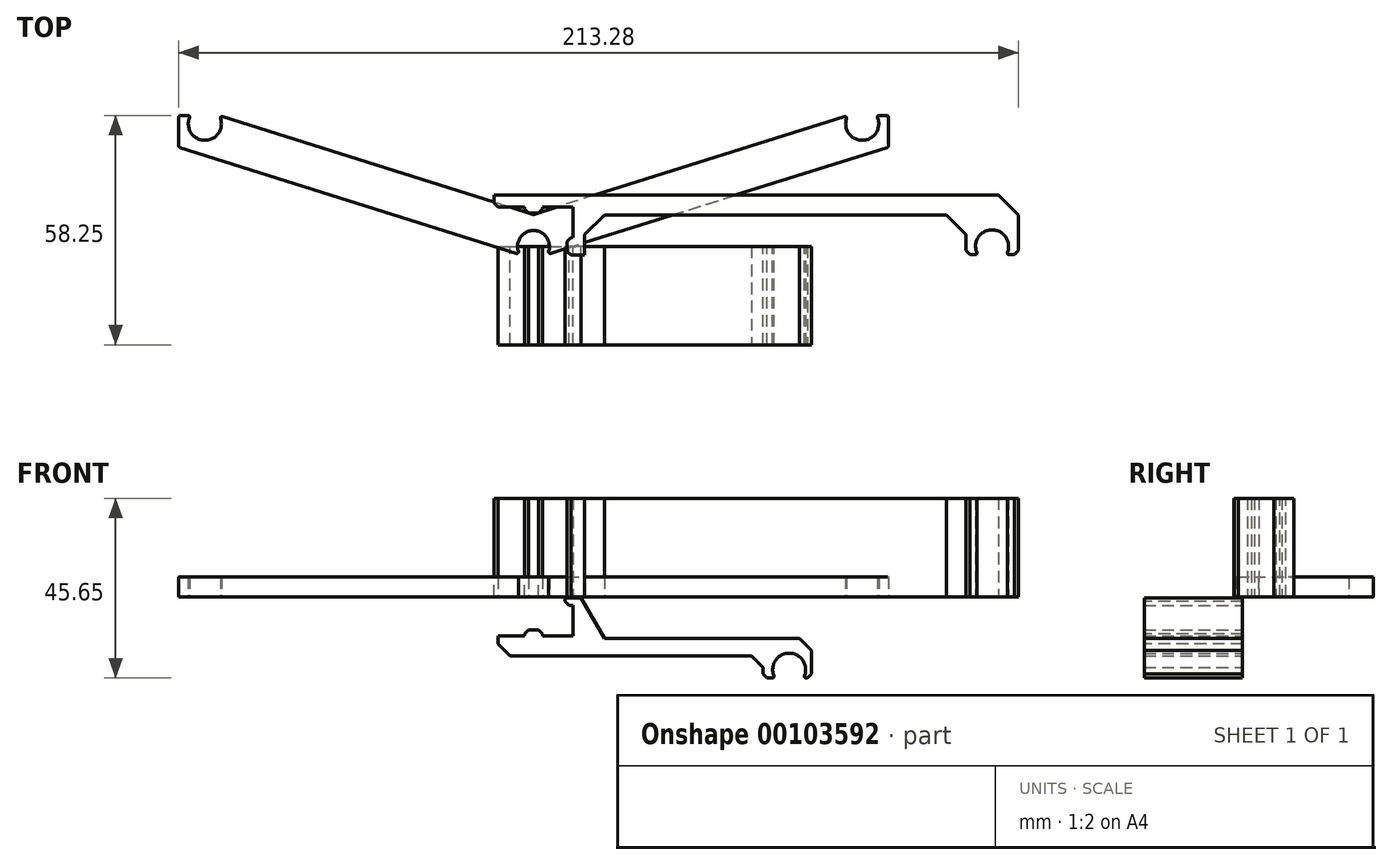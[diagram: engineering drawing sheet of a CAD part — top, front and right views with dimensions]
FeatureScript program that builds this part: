
annotation { "Feature Type Name" : "Feature", "Feature Type Description" : "" }
export const myFeature = defineFeature(function(context is Context, id is Id, definition is map)
    precondition{}
    {
        {
            var Q0;
            Q0=qCreatedBy(makeId("Front.planeOp"),FACE);
            var sketch = newSketch(context, id + "F0", { "sketchPlane" : qUnion([Q0])});
            skLineSegment(sketch, "E0.bottom", {"start": v(9, 10) * mm, "end": v(-9, 10) * mm});
            skLineSegment(sketch, "E0.top", {"start": v(9, -10) * mm, "end": v(-9, -10) * mm});
            skLineSegment(sketch, "E0.left", {"start": v(10, 9) * mm, "end": v(10, -9) * mm});
            skLineSegment(sketch, "E0.right", {"start": v(-10, 9) * mm, "end": v(-10, -9) * mm});
            skPoint(sketch, "E0.middle", {"position": v(0, 0) * mm});
            skPoint(sketch, "E1.visualSharp", {"position": v(10, 10) * mm});
            skArc(sketch, "E1.filletArc", {"start": v(10, 9) * mm, "mid": v(9.7, 9.7) * mm, "end": v(9, 10) * mm});
            skPoint(sketch, "E2.visualSharp", {"position": v(10, -10) * mm});
            skArc(sketch, "E2.filletArc", {"start": v(9, -10) * mm, "mid": v(9.7, -9.7) * mm, "end": v(10, -9) * mm});
            skPoint(sketch, "E3.visualSharp", {"position": v(-10, 10) * mm});
            skArc(sketch, "E3.filletArc", {"start": v(-9, 10) * mm, "mid": v(-9.7, 9.7) * mm, "end": v(-10, 9) * mm});
            skPoint(sketch, "E4.visualSharp", {"position": v(-10, -10) * mm});
            skArc(sketch, "E4.filletArc", {"start": v(-10, -9) * mm, "mid": v(-9.7, -9.7) * mm, "end": v(-9, -10) * mm});
            skLineSegment(sketch, "E5", {"start": v(10, 2.25) * mm, "end": v(8.5, 2.25) * mm});
            skLineSegment(sketch, "E6", {"start": v(8.5, 2.25) * mm, "end": v(8.5, 3.75) * mm});
            skLineSegment(sketch, "E7", {"start": v(8.5, 3.75) * mm, "end": v(4.45, 3.75) * mm});
            skLineSegment(sketch, "E8", {"start": v(10, -2.25) * mm, "end": v(8.5, -2.25) * mm});
            skLineSegment(sketch, "E9", {"start": v(8.5, -2.25) * mm, "end": v(8.5, -3.75) * mm});
            skLineSegment(sketch, "E10", {"start": v(8.5, -3.75) * mm, "end": v(4.45, -3.75) * mm});
            skArc(sketch, "E11", {"start": v(4.45, 3.75) * mm, "mid": v(3.3, 0) * mm, "end": v(4.45, -3.75) * mm});
            skLineSegment(sketch, "E12.1.0", {"start": v(-3.75, 8.5) * mm, "end": v(-3.75, 4.45) * mm});
            skArc(sketch, "E12.1.1", {"start": v(-3.75, 4.45) * mm, "mid": v(0, 3.3) * mm, "end": v(3.75, 4.45) * mm});
            skLineSegment(sketch, "E12.1.2", {"start": v(3.75, 8.5) * mm, "end": v(3.75, 4.45) * mm});
            skLineSegment(sketch, "E12.1.3", {"start": v(2.25, 8.5) * mm, "end": v(3.75, 8.5) * mm});
            skLineSegment(sketch, "E12.1.4", {"start": v(2.25, 10) * mm, "end": v(2.25, 8.5) * mm});
            skLineSegment(sketch, "E12.1.5", {"start": v(-2.25, 10) * mm, "end": v(-2.25, 8.5) * mm});
            skLineSegment(sketch, "E12.1.6", {"start": v(-2.25, 8.5) * mm, "end": v(-3.75, 8.5) * mm});
            skLineSegment(sketch, "E12.2.0", {"start": v(-8.5, -3.75) * mm, "end": v(-4.45, -3.75) * mm});
            skArc(sketch, "E12.2.1", {"start": v(-4.45, -3.75) * mm, "mid": v(-3.3, 0) * mm, "end": v(-4.45, 3.75) * mm});
            skLineSegment(sketch, "E12.2.2", {"start": v(-8.5, 3.75) * mm, "end": v(-4.45, 3.75) * mm});
            skLineSegment(sketch, "E12.2.3", {"start": v(-8.5, 2.25) * mm, "end": v(-8.5, 3.75) * mm});
            skLineSegment(sketch, "E12.2.4", {"start": v(-10, 2.25) * mm, "end": v(-8.5, 2.25) * mm});
            skLineSegment(sketch, "E12.2.5", {"start": v(-10, -2.25) * mm, "end": v(-8.5, -2.25) * mm});
            skLineSegment(sketch, "E12.2.6", {"start": v(-8.5, -2.25) * mm, "end": v(-8.5, -3.75) * mm});
            skLineSegment(sketch, "E12.3.0", {"start": v(3.75, -8.5) * mm, "end": v(3.75, -4.45) * mm});
            skArc(sketch, "E12.3.1", {"start": v(3.75, -4.45) * mm, "mid": v(0, -3.3) * mm, "end": v(-3.75, -4.45) * mm});
            skLineSegment(sketch, "E12.3.2", {"start": v(-3.75, -8.5) * mm, "end": v(-3.75, -4.45) * mm});
            skLineSegment(sketch, "E12.3.3", {"start": v(-2.25, -8.5) * mm, "end": v(-3.75, -8.5) * mm});
            skLineSegment(sketch, "E12.3.4", {"start": v(-2.25, -10) * mm, "end": v(-2.25, -8.5) * mm});
            skLineSegment(sketch, "E12.3.5", {"start": v(2.25, -10) * mm, "end": v(2.25, -8.5) * mm});
            skLineSegment(sketch, "E12.3.6", {"start": v(2.25, -8.5) * mm, "end": v(3.75, -8.5) * mm});
            skSolve(sketch);
        }
        {
            var Q0;
            Q0=qCreatedBy(makeId("Front.planeOp"),FACE);
            var sketch = newSketch(context, id + "F1", { "sketchPlane" : qUnion([Q0])});
            skLineSegment(sketch, "E13.0", {"start": v(10, -2.25) * mm, "end": v(8.5, -2.25) * mm, "construction": true});
            skLineSegment(sketch, "E14.0", {"start": v(10, 9) * mm, "end": v(10, -9) * mm, "construction": true});
            skLineSegment(sketch, "E15.0", {"start": v(9, -10) * mm, "end": v(-9, -10) * mm, "construction": true});
            skLineSegment(sketch, "E16.0", {"start": v(2.25, -10) * mm, "end": v(2.25, -8.5) * mm, "construction": true});
            skLineSegment(sketch, "E17.0", {"start": v(-2.25, -10) * mm, "end": v(-2.25, -8.5) * mm, "construction": true});
            skLineSegment(sketch, "E18", {"start": v(8, -2.25) * mm, "end": v(10, -2.25) * mm});
            skLineSegment(sketch, "E19", {"start": v(10, -2.25) * mm, "end": v(10, -10) * mm});
            skCircle(sketch, "E20", {"center": v(64.95, -18.55) * mm, "radius": 4.2 * mm});
            skLineSegment(sketch, "E21", {"start": v(-9, -10) * mm, "end": v(-9, -20.65) * mm});
            skLineSegment(sketch, "E22", {"start": v(-9, -20.65) * mm, "end": v(61.31, -20.65) * mm});
            skLineSegment(sketch, "E23", {"start": v(68.59, -20.65) * mm, "end": v(70.59, -20.65) * mm});
            skLineSegment(sketch, "E24", {"start": v(70.59, -20.65) * mm, "end": v(70.59, -10.65) * mm});
            skLineSegment(sketch, "E25", {"start": v(70.59, -10.65) * mm, "end": v(18, -10.65) * mm});
            skLineSegment(sketch, "E26", {"start": v(18, -10.65) * mm, "end": v(12, -0.25) * mm});
            skLineSegment(sketch, "E27", {"start": v(12, -0.25) * mm, "end": v(8, -0.25) * mm});
            skLineSegment(sketch, "E28", {"start": v(8, -0.25) * mm, "end": v(8, -2.25) * mm});
            skLineSegment(sketch, "E29", {"start": v(-9, -15) * mm, "end": v(58.31, -15) * mm});
            skLineSegment(sketch, "E30", {"start": v(58.31, -15) * mm, "end": v(58.31, -20.65) * mm});
            skLineSegment(sketch, "E31", {"start": v(64.95, -18.55) * mm, "end": v(61.31, -20.65) * mm, "construction": true});
            skLineSegment(sketch, "E32", {"start": v(64.95, -18.55) * mm, "end": v(68.59, -20.65) * mm, "construction": true});
            skLineSegment(sketch, "E33", {"start": v(60.75, -18.55) * mm, "end": v(69.15, -18.55) * mm, "construction": true});
            skLineSegment(sketch, "E34", {"start": v(-9, -10) * mm, "end": v(-2.25, -10) * mm});
            skLineSegment(sketch, "E35", {"start": v(-2.25, -10) * mm, "end": v(-2.25, -8.5) * mm});
            skLineSegment(sketch, "E36", {"start": v(-2.25, -8.5) * mm, "end": v(2.25, -8.5) * mm});
            skLineSegment(sketch, "E37", {"start": v(2.25, -8.5) * mm, "end": v(2.25, -10) * mm});
            skLineSegment(sketch, "E38", {"start": v(2.25, -10) * mm, "end": v(10, -10) * mm});
            skSolve(sketch);
        }
        {
            var Q0;
            Q0=makeQuery(id+"F1.imprint","IMPRINT",FACE,{"disambiguationData":[TD([[makeQuery(id+"F1.imprint","IMPRINT",EDGE,{"derivedFrom":sQuery(id+"F1.wireOp",EDGE,"E18")}),1.0]])]});
            extrude(context, id + "F2", {"entities" : qUnion([Q0]), "depth" : 25 * mm});
        }
        {
            var Q0;
            Q0=makeQuery(id+"F2.opExtrude","SWEPT_EDGE",EDGE,{"disambiguationData":[OSD([sQuery(id+"F1.wireOp",EDGE,"E35"),sQuery(id+"F1.wireOp",EDGE,"E36")])]});
            var Q1;
            Q1=makeQuery(id+"F2.opExtrude","SWEPT_EDGE",EDGE,{"disambiguationData":[OSD([sQuery(id+"F1.wireOp",EDGE,"E36"),sQuery(id+"F1.wireOp",EDGE,"E37")])]});
            var Q2;
            Q2=makeQuery(id+"F2.opExtrude","SWEPT_EDGE",EDGE,{"disambiguationData":[OSD([sQuery(id+"F1.wireOp",EDGE,"E18"),sQuery(id+"F1.wireOp",EDGE,"E28")])]});
            var Q3;
            Q3=makeQuery(id+"F2.opExtrude","SWEPT_EDGE",EDGE,{"disambiguationData":[OSD([sQuery(id+"F1.wireOp",EDGE,"E22"),sQuery(id+"F1.wireOp",EDGE,"E30")])]});
            var Q4;
            Q4=makeQuery(id+"F2.opExtrude","SWEPT_EDGE",EDGE,{"disambiguationData":[OSD([sQuery(id+"F1.wireOp",EDGE,"E23"),sQuery(id+"F1.wireOp",EDGE,"E24")])]});
            chamfer(context, id + "F3", {"entities" : qUnion([Q0, Q1, Q2, Q3, Q4]), "width" : 1 * mm, "tangentPropagation" : true});
        }
        {
            var Q0;
            Q0=makeQuery(id+"F2.opExtrude","SWEPT_EDGE",EDGE,{"disambiguationData":[OSD([sQuery(id+"F1.wireOp",EDGE,"E21"),sQuery(id+"F1.wireOp",EDGE,"E29")])]});
            var Q1;
            Q1=makeQuery(id+"F2.opExtrude","SWEPT_EDGE",EDGE,{"disambiguationData":[OSD([sQuery(id+"F1.wireOp",EDGE,"E29"),sQuery(id+"F1.wireOp",EDGE,"E30")])]});
            var Q2;
            Q2=makeQuery(id+"F2.opExtrude","SWEPT_EDGE",EDGE,{"disambiguationData":[OSD([sQuery(id+"F1.wireOp",EDGE,"E24"),sQuery(id+"F1.wireOp",EDGE,"E25")])]});
            chamfer(context, id + "F4", {"entities" : qUnion([Q0, Q1, Q2]), "width" : 3 * mm, "tangentPropagation" : true});
        }
        {
            var Q0;
            Q0=qCreatedBy(makeId("Top.planeOp"),FACE);
            var sketch = newSketch(context, id + "F5", { "sketchPlane" : qUnion([Q0])});
            skLineSegment(sketch, "E39.bottom", {"start": v(10, 10) * mm, "end": v(-10, 10) * mm, "construction": true});
            skLineSegment(sketch, "E39.top", {"start": v(10, -10) * mm, "end": v(-10, -10) * mm, "construction": true});
            skLineSegment(sketch, "E39.left", {"start": v(10, 10) * mm, "end": v(10, -10) * mm, "construction": true});
            skLineSegment(sketch, "E39.right", {"start": v(-10, 10) * mm, "end": v(-10, -10) * mm, "construction": true});
            skPoint(sketch, "E39.middle", {"position": v(0, 0) * mm});
            skCircle(sketch, "E40", {"center": v(116.5, 0) * mm, "radius": 4.2 * mm});
            skLineSegment(sketch, "E41", {"start": v(-10, 10) * mm, "end": v(-10, 13) * mm});
            skLineSegment(sketch, "E42", {"start": v(-10, 13) * mm, "end": v(123.14, 13) * mm});
            skLineSegment(sketch, "E43", {"start": v(123.14, 13) * mm, "end": v(123.14, -2.1) * mm});
            skLineSegment(sketch, "E44", {"start": v(123.14, -2.1) * mm, "end": v(120.14, -2.1) * mm});
            skLineSegment(sketch, "E45", {"start": v(112.86, -2.1) * mm, "end": v(109.86, -2.1) * mm});
            skLineSegment(sketch, "E46", {"start": v(109.86, -2.1) * mm, "end": v(109.86, 8) * mm});
            skLineSegment(sketch, "E47", {"start": v(109.86, 8) * mm, "end": v(13, 8) * mm});
            skLineSegment(sketch, "E48", {"start": v(13, 8) * mm, "end": v(13, -2.25) * mm});
            skLineSegment(sketch, "E49", {"start": v(13, -2.25) * mm, "end": v(10, -2.25) * mm});
            skLineSegment(sketch, "E50", {"start": v(10, -2.25) * mm, "end": v(8.5, -2.25) * mm});
            skLineSegment(sketch, "E51", {"start": v(8.5, -2.25) * mm, "end": v(8.5, 2.25) * mm});
            skLineSegment(sketch, "E52", {"start": v(8.5, 2.25) * mm, "end": v(10, 2.25) * mm});
            skLineSegment(sketch, "E53", {"start": v(10, 2.25) * mm, "end": v(10, 10) * mm});
            skLineSegment(sketch, "E54", {"start": v(10, 10) * mm, "end": v(2.25, 10) * mm});
            skLineSegment(sketch, "E55", {"start": v(2.25, 10) * mm, "end": v(2.25, 8.5) * mm});
            skLineSegment(sketch, "E56", {"start": v(2.25, 8.5) * mm, "end": v(-2.25, 8.5) * mm});
            skLineSegment(sketch, "E57", {"start": v(-2.25, 8.5) * mm, "end": v(-2.25, 10) * mm});
            skLineSegment(sketch, "E58", {"start": v(-2.25, 10) * mm, "end": v(-10, 10) * mm});
            skLineSegment(sketch, "E59", {"start": v(112.3, 0) * mm, "end": v(120.7, 0) * mm, "construction": true});
            skLineSegment(sketch, "E60", {"start": v(116.5, 0) * mm, "end": v(112.86, -2.1) * mm, "construction": true});
            skLineSegment(sketch, "E61", {"start": v(116.5, 0) * mm, "end": v(120.14, -2.1) * mm, "construction": true});
            skSolve(sketch);
        }
        {
            var Q0;
            Q0=makeQuery(id+"F5.imprint","IMPRINT",FACE,{"disambiguationData":[TD([[makeQuery(id+"F5.imprint","IMPRINT",EDGE,{"derivedFrom":sQuery(id+"F5.wireOp",EDGE,"E41")}),-1.0]])]});
            extrude(context, id + "F6", {"entities" : qUnion([Q0]), "depth" : 25 * mm});
        }
        {
            var Q0;
            Q0=makeQuery(id+"F6.opExtrude","SWEPT_EDGE",EDGE,{"disambiguationData":[OSD([sQuery(id+"F5.wireOp",EDGE,"E51"),sQuery(id+"F5.wireOp",EDGE,"E52")])]});
            var Q1;
            Q1=makeQuery(id+"F6.opExtrude","SWEPT_EDGE",EDGE,{"disambiguationData":[OSD([sQuery(id+"F5.wireOp",EDGE,"E50"),sQuery(id+"F5.wireOp",EDGE,"E51")])]});
            var Q2;
            Q2=makeQuery(id+"F6.opExtrude","SWEPT_EDGE",EDGE,{"disambiguationData":[OSD([sQuery(id+"F5.wireOp",EDGE,"E56"),sQuery(id+"F5.wireOp",EDGE,"E57")])]});
            var Q3;
            Q3=makeQuery(id+"F6.opExtrude","SWEPT_EDGE",EDGE,{"disambiguationData":[OSD([sQuery(id+"F5.wireOp",EDGE,"E55"),sQuery(id+"F5.wireOp",EDGE,"E56")])]});
            var Q4;
            Q4=makeQuery(id+"F6.opExtrude","SWEPT_EDGE",EDGE,{"disambiguationData":[OSD([sQuery(id+"F5.wireOp",EDGE,"E41"),sQuery(id+"F5.wireOp",EDGE,"E58")])]});
            var Q5;
            Q5=makeQuery(id+"F6.opExtrude","SWEPT_EDGE",EDGE,{"disambiguationData":[OSD([sQuery(id+"F5.wireOp",EDGE,"E45"),sQuery(id+"F5.wireOp",EDGE,"E46")])]});
            var Q6;
            Q6=makeQuery(id+"F6.opExtrude","SWEPT_EDGE",EDGE,{"disambiguationData":[OSD([sQuery(id+"F5.wireOp",EDGE,"E43"),sQuery(id+"F5.wireOp",EDGE,"E44")])]});
            chamfer(context, id + "F7", {"entities" : qUnion([Q0, Q1, Q2, Q3, Q4, Q5, Q6]), "width" : 1 * mm, "tangentPropagation" : true});
        }
        {
            var Q0;
            Q0=makeQuery(id+"F6.opExtrude","SWEPT_EDGE",EDGE,{"disambiguationData":[OSD([sQuery(id+"F5.wireOp",EDGE,"E42"),sQuery(id+"F5.wireOp",EDGE,"E43")])]});
            var Q1;
            Q1=makeQuery(id+"F6.opExtrude","SWEPT_EDGE",EDGE,{"disambiguationData":[OSD([sQuery(id+"F5.wireOp",EDGE,"E46"),sQuery(id+"F5.wireOp",EDGE,"E47")])]});
            var Q2;
            Q2=makeQuery(id+"F6.opExtrude","SWEPT_EDGE",EDGE,{"disambiguationData":[OSD([sQuery(id+"F5.wireOp",EDGE,"E47"),sQuery(id+"F5.wireOp",EDGE,"E48")])]});
            chamfer(context, id + "F8", {"entities" : qUnion([Q0, Q1, Q2]), "width" : 5 * mm, "tangentPropagation" : true});
        }
        {
            var Q0;
            Q0=makeQuery(id+"F2.opExtrude","SWEPT_EDGE",EDGE,{"disambiguationData":[OSD([sQuery(id+"F1.wireOp",EDGE,"E20"),sQuery(id+"F1.wireOp",EDGE,"E22")])]});
            var Q1;
            Q1=makeQuery(id+"F2.opExtrude","SWEPT_EDGE",EDGE,{"disambiguationData":[OSD([sQuery(id+"F1.wireOp",EDGE,"E20"),sQuery(id+"F1.wireOp",EDGE,"E23")])]});
            var Q2;
            Q2=makeQuery(id+"F6.opExtrude","SWEPT_EDGE",EDGE,{"disambiguationData":[OSD([sQuery(id+"F5.wireOp",EDGE,"E40"),sQuery(id+"F5.wireOp",EDGE,"E45")])]});
            var Q3;
            Q3=makeQuery(id+"F6.opExtrude","SWEPT_EDGE",EDGE,{"disambiguationData":[OSD([sQuery(id+"F5.wireOp",EDGE,"E40"),sQuery(id+"F5.wireOp",EDGE,"E44")])]});
            fillet(context, id + "F9", {"entities" : qUnion([Q0, Q1, Q2, Q3]), "radius" : 0.4 * mm, "tangentPropagation" : true, "allowEdgeOverflow" : false});
        }
        {
            var Q0;
            Q0=qCreatedBy(makeId("Top.planeOp"),FACE);
            var sketch = newSketch(context, id + "F10", { "sketchPlane" : qUnion([Q0])});
            skCircle(sketch, "E62", {"center": v(0, 0) * mm, "radius": 4.05 * mm});
            skCircle(sketch, "E63", {"center": v(-83.5, 31.15) * mm, "radius": 4.2 * mm});
            skLineSegment(sketch, "E64", {"start": v(0, 0) * mm, "end": v(0, 66.48) * mm, "construction": true});
            skCircle(sketch, "E65.MirrorC", {"center": v(83.5, 31.15) * mm, "radius": 4.2 * mm});
            skLineSegment(sketch, "E66", {"start": v(-79.3, 31.15) * mm, "end": v(-87.7, 31.15) * mm, "construction": true});
            skLineSegment(sketch, "E67", {"start": v(-4.05, 0) * mm, "end": v(4.05, 0) * mm, "construction": true});
            skLineSegment(sketch, "E68", {"start": v(-83.5, 31.15) * mm, "end": v(-87.14, 33.25) * mm, "construction": true});
            skLineSegment(sketch, "E69", {"start": v(-83.5, 31.15) * mm, "end": v(-79.86, 33.25) * mm, "construction": true});
            skLineSegment(sketch, "E70", {"start": v(0, 0) * mm, "end": v(-3.5, -2.02) * mm, "construction": true});
            skLineSegment(sketch, "E71", {"start": v(0, 0) * mm, "end": v(3.5, -2.02) * mm, "construction": true});
            skLineSegment(sketch, "E72", {"start": v(-87.14, 33.25) * mm, "end": v(-90.14, 33.25) * mm});
            skLineSegment(sketch, "E73", {"start": v(-90.14, 33.25) * mm, "end": v(-90.14, 25.25) * mm});
            skLineSegment(sketch, "E74", {"start": v(-90.14, 25.25) * mm, "end": v(-90.14, 25.25) * mm});
            skLineSegment(sketch, "E75", {"start": v(-3.5, -2.03) * mm, "end": v(-90.14, 25.25) * mm});
            skLineSegment(sketch, "E76", {"start": v(-79.86, 33.25) * mm, "end": v(0, 8.1) * mm});
            skLineSegment(sketch, "E77.MirrorCS", {"start": v(79.86, 33.25) * mm, "end": v(0, 8.1) * mm});
            skLineSegment(sketch, "E78.MirrorCS", {"start": v(3.5, -2.03) * mm, "end": v(90.14, 25.25) * mm});
            skLineSegment(sketch, "E79.MirrorCS", {"start": v(90.14, 33.25) * mm, "end": v(90.14, 25.25) * mm});
            skLineSegment(sketch, "E80.MirrorCS", {"start": v(83.5, 31.15) * mm, "end": v(79.86, 33.25) * mm, "construction": true});
            skLineSegment(sketch, "E81.MirrorCS", {"start": v(83.5, 31.15) * mm, "end": v(87.14, 33.25) * mm, "construction": true});
            skLineSegment(sketch, "E82.MirrorCS", {"start": v(87.14, 33.25) * mm, "end": v(90.14, 33.25) * mm});
            skSolve(sketch);
        }
        {
            var Q0;
            {var subQ5=sQuery(id+"F10.wireOp",EDGE,"E72");Q0=makeQuery(id+"F10.imprint","IMPRINT",FACE,{"disambiguationData":[TD([[makeQuery(id+"F10.imprint","IMPRINT",EDGE,{"derivedFrom":subQ5}),1.0]])]});}
            extrude(context, id + "F11", {"entities" : qUnion([Q0]), "depth" : 5 * mm});
        }
        {
            var Q0;
            Q0=makeQuery(id+"F11.opExtrude","SWEPT_EDGE",EDGE,{"disambiguationData":[OSD([sQuery(id+"F10.wireOp",EDGE,"E62"),sQuery(id+"F10.wireOp",EDGE,"E75")])]});
            var Q1;
            Q1=makeQuery(id+"F11.opExtrude","SWEPT_EDGE",EDGE,{"disambiguationData":[OSD([sQuery(id+"F10.wireOp",EDGE,"E62"),sQuery(id+"F10.wireOp",EDGE,"E78.MirrorCS")])]});
            var Q2;
            Q2=makeQuery(id+"F11.opExtrude","SWEPT_EDGE",EDGE,{"disambiguationData":[OSD([sQuery(id+"F10.wireOp",EDGE,"E76"),sQuery(id+"F10.wireOp",EDGE,"E77.MirrorCS")])]});
            var Q3;
            Q3=makeQuery(id+"F11.opExtrude","SWEPT_EDGE",EDGE,{"disambiguationData":[OSD([sQuery(id+"F10.wireOp",EDGE,"E65.MirrorC"),sQuery(id+"F10.wireOp",EDGE,"E77.MirrorCS")])]});
            var Q4;
            Q4=makeQuery(id+"F11.opExtrude","SWEPT_EDGE",EDGE,{"disambiguationData":[OSD([sQuery(id+"F10.wireOp",EDGE,"E65.MirrorC"),sQuery(id+"F10.wireOp",EDGE,"E82.MirrorCS")])]});
            var Q5;
            Q5=makeQuery(id+"F11.opExtrude","SWEPT_EDGE",EDGE,{"disambiguationData":[OSD([sQuery(id+"F10.wireOp",EDGE,"E79.MirrorCS"),sQuery(id+"F10.wireOp",EDGE,"E82.MirrorCS")])]});
            var Q6;
            Q6=makeQuery(id+"F11.opExtrude","SWEPT_EDGE",EDGE,{"disambiguationData":[OSD([sQuery(id+"F10.wireOp",EDGE,"E78.MirrorCS"),sQuery(id+"F10.wireOp",EDGE,"E79.MirrorCS")])]});
            var Q7;
            Q7=makeQuery(id+"F11.opExtrude","SWEPT_EDGE",EDGE,{"disambiguationData":[OSD([sQuery(id+"F10.wireOp",EDGE,"E72"),sQuery(id+"F10.wireOp",EDGE,"E73")])]});
            var Q8;
            Q8=makeQuery(id+"F11.opExtrude","SWEPT_EDGE",EDGE,{"disambiguationData":[OSD([sQuery(id+"F10.wireOp",EDGE,"E73"),sQuery(id+"F10.wireOp",EDGE,"E75")])]});
            var Q9;
            Q9=makeQuery(id+"F11.opExtrude","SWEPT_EDGE",EDGE,{"disambiguationData":[OSD([sQuery(id+"F10.wireOp",EDGE,"E63"),sQuery(id+"F10.wireOp",EDGE,"E76")])]});
            var Q10;
            Q10=makeQuery(id+"F11.opExtrude","SWEPT_EDGE",EDGE,{"disambiguationData":[OSD([sQuery(id+"F10.wireOp",EDGE,"E63"),sQuery(id+"F10.wireOp",EDGE,"E72")])]});
            fillet(context, id + "F12", {"entities" : qUnion([Q0, Q1, Q2, Q3, Q4, Q5, Q6, Q7, Q8, Q9, Q10]), "radius" : 0.4 * mm, "tangentPropagation" : true, "allowEdgeOverflow" : false});
        }
    });
